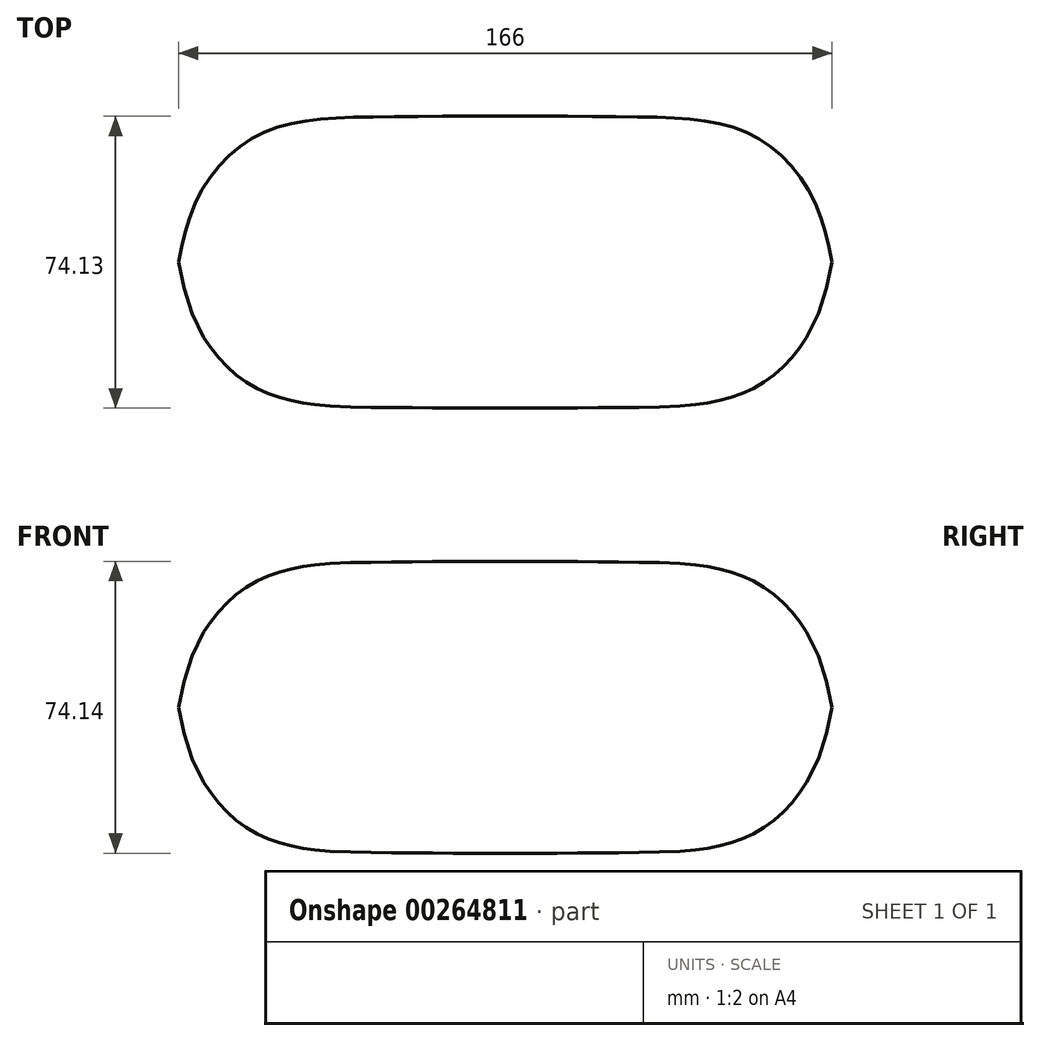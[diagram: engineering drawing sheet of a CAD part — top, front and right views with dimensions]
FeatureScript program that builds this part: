
annotation { "Feature Type Name" : "Feature", "Feature Type Description" : "" }
export const myFeature = defineFeature(function(context is Context, id is Id, definition is map)
    precondition{}
    {
        {
            var Q0;
            Q0=qCreatedBy(makeId("Top.planeOp"),FACE);
            var sketch = newSketch(context, id + "F0", { "sketchPlane" : qUnion([Q0])});
            skLineSegment(sketch, "E0", {"start": v(-80.2, 46.21) * mm, "end": v(85.8, 46.21) * mm});
            skFitSpline(sketch, "E1", {"points": [v(-80.2, 46.21) * mm, v(-76.73, 59.42) * mm, v(-69.78, 70.77) * mm, v(-60.51, 78.18) * mm, v(-49.16, 81.9) * mm, v(-33.64, 83.05) * mm, v(0, 83.28) * mm], "startDerivative": vector(17.46, 87.44) * mm, "endDerivative": vector(152.13, 0.22) * mm});
            skLineSegment(sketch, "E2", {"start": v(-80.2, 46.21) * mm, "end": v(2.8, 46.21) * mm, "construction": true});
            skLineSegment(sketch, "E3", {"start": v(2.8, 46.21) * mm, "end": v(2.8, 83.28) * mm, "construction": true});
            skFitSpline(sketch, "E4.MirrorCS", {"points": [v(85.8, 46.21) * mm, v(82.32, 59.42) * mm, v(75.37, 70.77) * mm, v(66.1, 78.18) * mm, v(54.75, 81.9) * mm, v(39.23, 83.05) * mm, v(5.6, 83.28) * mm], "startDerivative": vector(-17.46, 87.44) * mm, "endDerivative": vector(-152.13, 0.22) * mm});
            skLineSegment(sketch, "E5", {"start": v(5.6, 83.28) * mm, "end": v(0, 83.28) * mm});
            skSolve(sketch);
        }
        {
            var Q0;
            {var subQ0=sQuery(id+"F0.wireOp",EDGE,"E1");Q0=makeQuery(id+"F0.imprint","IMPRINT",FACE,{"disambiguationData":[TD([[makeQuery(id+"F0.imprint","IMPRINT",EDGE,{"derivedFrom":subQ0}),-1.0]])]});}
            var Q1;
            Q1=sQuery(id+"F0.wireOp",EDGE,"E0");
            revolve(context, id + "F1", {"entities" : qUnion([Q0]), "axis" : qUnion([Q1]), "revolveType" : RevolveType.FULL});
        }
    });
